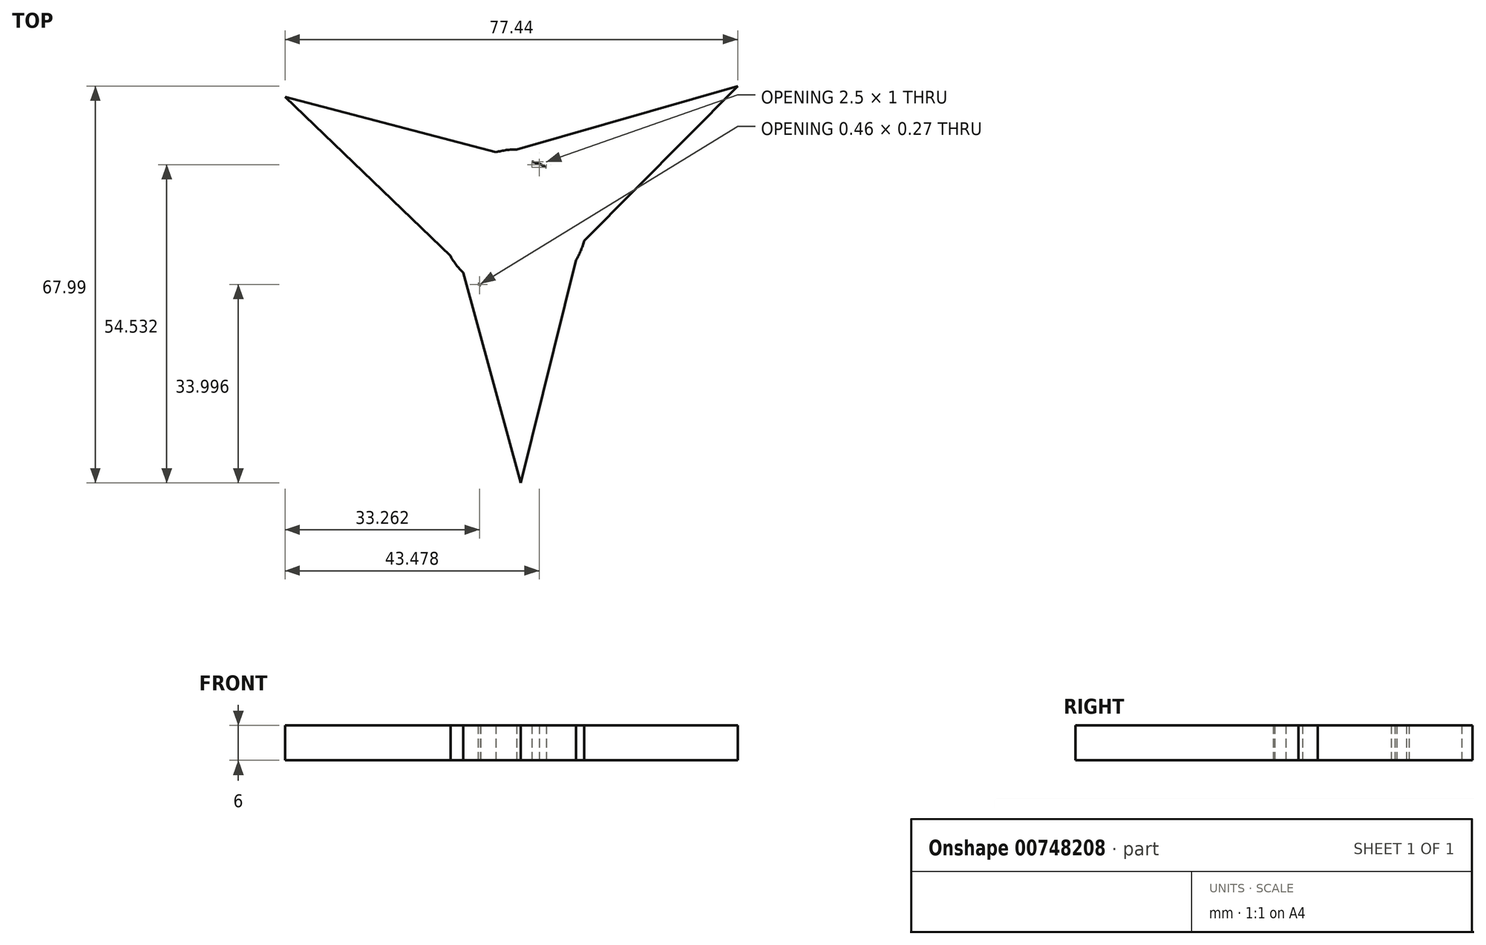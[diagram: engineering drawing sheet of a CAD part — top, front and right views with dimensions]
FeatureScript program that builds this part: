
annotation { "Feature Type Name" : "Feature", "Feature Type Description" : "" }
export const myFeature = defineFeature(function(context is Context, id is Id, definition is map)
    precondition{}
    {
        {
            var Q0;
            Q0=qCreatedBy(makeId("Top.planeOp"),FACE);
            var sketch = newSketch(context, id + "F0", { "sketchPlane" : qUnion([Q0])});
            skCircle(sketch, "E0", {"center": v(0.18, 0.31) * mm, "radius": 11 * mm});
            skCircle(sketch, "E1", {"center": v(0.18, 0.31) * mm, "radius": 12.1 * mm});
            skLineSegment(sketch, "E2", {"start": v(-5.66, -10.27) * mm, "end": v(-0.97, -34.05) * mm});
            skLineSegment(sketch, "E3", {"start": v(-0.97, -34.05) * mm, "end": v(1.1, -22.16) * mm});
            skPoint(sketch, "E3.endSnap0", {"position": v(-3.32, -22.16) * mm});
            skLineSegment(sketch, "E4", {"start": v(1.1, -22.16) * mm, "end": v(3.44, -34.05) * mm});
            skLineSegment(sketch, "E5", {"start": v(3.44, -34.05) * mm, "end": v(8.37, -5.81) * mm});
            skLineSegment(sketch, "E6", {"start": v(-11.75, 2.26) * mm, "end": v(1.06, -44.71) * mm});
            skLineSegment(sketch, "E7", {"start": v(1.06, -44.71) * mm, "end": v(12.28, 0.44) * mm});
            skLineSegment(sketch, "E8.1.0", {"start": v(38.2, 23.28) * mm, "end": v(-6.52, 10.41) * mm});
            skLineSegment(sketch, "E8.1.1", {"start": v(3.91, -11.3) * mm, "end": v(38.2, 23.28) * mm});
            skLineSegment(sketch, "E8.1.2", {"start": v(27.77, 20) * mm, "end": v(0.85, 10.15) * mm});
            skLineSegment(sketch, "E8.1.3", {"start": v(18.64, 12.03) * mm, "end": v(27.77, 20) * mm});
            skLineSegment(sketch, "E8.1.4", {"start": v(29.97, 16.18) * mm, "end": v(18.64, 12.03) * mm});
            skLineSegment(sketch, "E8.1.5", {"start": v(11.73, 0.23) * mm, "end": v(29.97, 16.18) * mm});
            skCircle(sketch, "E8.1.6", {"center": v(-0.36, 0) * mm, "radius": 12.1 * mm});
            skCircle(sketch, "E8.1.7", {"center": v(-0.36, 0) * mm, "radius": 11 * mm});
            skPoint(sketch, "E8.1.8", {"position": v(20.85, 8.2) * mm});
            skLineSegment(sketch, "E8.2.0", {"start": v(-39.25, 21.44) * mm, "end": v(-5.76, -10.85) * mm});
            skLineSegment(sketch, "E8.2.1", {"start": v(7.83, 9.04) * mm, "end": v(-39.25, 21.44) * mm});
            skLineSegment(sketch, "E8.2.2", {"start": v(-31.2, 14.04) * mm, "end": v(-9.22, -4.34) * mm});
            skLineSegment(sketch, "E8.2.3", {"start": v(-19.74, 10.13) * mm, "end": v(-31.2, 14.04) * mm});
            skLineSegment(sketch, "E8.2.4", {"start": v(-29, 17.87) * mm, "end": v(-19.74, 10.13) * mm});
            skLineSegment(sketch, "E8.2.5", {"start": v(-6.06, 10.04) * mm, "end": v(-29, 17.87) * mm});
            skCircle(sketch, "E8.2.6", {"center": v(0.18, -0.32) * mm, "radius": 12.1 * mm});
            skCircle(sketch, "E8.2.7", {"center": v(0.18, -0.32) * mm, "radius": 11 * mm});
            skPoint(sketch, "E8.2.8", {"position": v(-17.53, 13.95) * mm});
            skPoint(sketch, "E8.center", {"position": v(0, 0) * mm});
            skSolve(sketch);
        }
        {
            var Q0;
            {var subQ14=sQuery(id+"F0.wireOp",EDGE,"E8.1.3");Q0=makeQuery(id+"F0.imprint","IMPRINT",FACE,{"disambiguationData":[TD([[makeQuery(id+"F0.imprint","IMPRINT",EDGE,{"derivedFrom":subQ14}),-1.0]])]});}
            var Q1;
            {var subQ1=sQuery(id+"F0.wireOp",EDGE,"E8.1.3");Q1=makeQuery(id+"F0.imprint","IMPRINT",FACE,{"disambiguationData":[TD([[makeQuery(id+"F0.imprint","IMPRINT",EDGE,{"derivedFrom":subQ1}),1.0]])]});}
            var Q2;
            {var subQ4=sQuery(id+"F0.wireOp",EDGE,"E3");Q2=makeQuery(id+"F0.imprint","IMPRINT",FACE,{"disambiguationData":[TD([[makeQuery(id+"F0.imprint","IMPRINT",EDGE,{"derivedFrom":subQ4}),1.0]])]});}
            var Q3;
            {var subQ0=sQuery(id+"F0.wireOp",EDGE,"E8.2.3");Q3=makeQuery(id+"F0.imprint","IMPRINT",FACE,{"disambiguationData":[TD([[makeQuery(id+"F0.imprint","IMPRINT",EDGE,{"derivedFrom":subQ0}),1.0]])]});}
            var Q4;
            {var subQ1=sQuery(id+"F0.wireOp",EDGE,"E0");var subQ6=sQuery(id+"F0.wireOp",EDGE,"E8.2.7");var subQ7=makeQuery(id+"F0.imprint","INTERSECT",VERTEX,{"disambiguationData":[OD(0.0)],"derivedFrom":[subQ1,subQ6]});Q4=makeQuery(id+"F0.imprint","IMPRINT",FACE,{"disambiguationData":[TD([[makeQuery(id+"F0.imprint","IMPRINT",EDGE,{"disambiguationData":[TD([[subQ7,-1.0]])],"derivedFrom":subQ1}),1.0]])]});}
            var Q5;
            {var subQ6=sQuery(id+"F0.wireOp",EDGE,"E8.2.3");Q5=makeQuery(id+"F0.imprint","IMPRINT",FACE,{"disambiguationData":[TD([[makeQuery(id+"F0.imprint","IMPRINT",EDGE,{"derivedFrom":subQ6}),-1.0]])]});}
            var Q6;
            {var subQ0=sQuery(id+"F0.wireOp",EDGE,"E8.1.6");var subQ1=sQuery(id+"F0.wireOp",EDGE,"E6");var subQ2=makeQuery(id+"F0.imprint","INTERSECT",VERTEX,{"derivedFrom":[subQ1,subQ0]});Q6=makeQuery(id+"F0.imprint","IMPRINT",FACE,{"disambiguationData":[TD([[makeQuery(id+"F0.imprint","IMPRINT",EDGE,{"disambiguationData":[TD([[subQ2,1.0]])],"derivedFrom":subQ1}),-1.0]])]});}
            var Q7;
            {var subQ7=sQuery(id+"F0.wireOp",EDGE,"E3");Q7=makeQuery(id+"F0.imprint","IMPRINT",FACE,{"disambiguationData":[TD([[makeQuery(id+"F0.imprint","IMPRINT",EDGE,{"derivedFrom":subQ7}),-1.0]])]});}
            var Q8;
            {var subQ0=sQuery(id+"F0.wireOp",EDGE,"E8.2.2");var subQ1=sQuery(id+"F0.wireOp",EDGE,"E6");var subQ2=makeQuery(id+"F0.imprint","INTERSECT",VERTEX,{"derivedFrom":[subQ1,subQ0]});Q8=makeQuery(id+"F0.imprint","IMPRINT",FACE,{"disambiguationData":[TD([[makeQuery(id+"F0.imprint","IMPRINT",EDGE,{"disambiguationData":[TD([[subQ2,-1.0]])],"derivedFrom":subQ1}),-1.0]])]});}
            var Q9;
            {var subQ7=sQuery(id+"F0.wireOp",EDGE,"E1");var subQ8=makeQuery(id+"F0.imprint","INTERSECT",VERTEX,{"disambiguationData":[OD(0.0)],"derivedFrom":[subQ7,sQuery(id+"F0.wireOp",EDGE,"E6")]});Q9=makeQuery(id+"F0.imprint","IMPRINT",FACE,{"disambiguationData":[TD([[makeQuery(id+"F0.imprint","IMPRINT",EDGE,{"disambiguationData":[TD([[subQ8,1.0]])],"derivedFrom":subQ7}),-1.0]])]});}
            var Q10;
            {var subQ0=sQuery(id+"F0.wireOp",EDGE,"E8.1.7");var subQ1=sQuery(id+"F0.wireOp",EDGE,"E0");var subQ2=makeQuery(id+"F0.imprint","INTERSECT",VERTEX,{"disambiguationData":[OD(1.0)],"derivedFrom":[subQ1,subQ0]});Q10=makeQuery(id+"F0.imprint","IMPRINT",FACE,{"disambiguationData":[TD([[makeQuery(id+"F0.imprint","IMPRINT",EDGE,{"disambiguationData":[TD([[subQ2,-1.0]])],"derivedFrom":subQ1}),-1.0]])]});}
            var Q11;
            {var subQ0=sQuery(id+"F0.wireOp",EDGE,"E8.2.2");var subQ1=sQuery(id+"F0.wireOp",EDGE,"E0");var subQ2=makeQuery(id+"F0.imprint","INTERSECT",VERTEX,{"derivedFrom":[subQ1,subQ0]});Q11=makeQuery(id+"F0.imprint","IMPRINT",FACE,{"disambiguationData":[TD([[makeQuery(id+"F0.imprint","IMPRINT",EDGE,{"disambiguationData":[TD([[subQ2,-1.0]])],"derivedFrom":subQ1}),-1.0]])]});}
            var Q12;
            {var subQ6=sQuery(id+"F0.wireOp",EDGE,"E8.2.1");var subQ8=sQuery(id+"F0.wireOp",EDGE,"E0");var subQ9=makeQuery(id+"F0.imprint","INTERSECT",VERTEX,{"disambiguationData":[OD(0.0)],"derivedFrom":[subQ8,subQ6]});Q12=makeQuery(id+"F0.imprint","IMPRINT",FACE,{"disambiguationData":[TD([[makeQuery(id+"F0.imprint","IMPRINT",EDGE,{"disambiguationData":[TD([[subQ9,1.0]])],"derivedFrom":subQ8}),-1.0]])]});}
            var Q13;
            {var subQ0=sQuery(id+"F0.wireOp",EDGE,"E8.1.1");var subQ1=sQuery(id+"F0.wireOp",EDGE,"E1");var subQ2=makeQuery(id+"F0.imprint","INTERSECT",VERTEX,{"disambiguationData":[OD(0.0)],"derivedFrom":[subQ1,subQ0]});Q13=makeQuery(id+"F0.imprint","IMPRINT",FACE,{"disambiguationData":[TD([[makeQuery(id+"F0.imprint","IMPRINT",EDGE,{"disambiguationData":[TD([[subQ2,-1.0]])],"derivedFrom":subQ1}),-1.0]])]});}
            var Q14;
            {var subQ0=sQuery(id+"F0.wireOp",EDGE,"E7");var subQ1=sQuery(id+"F0.wireOp",EDGE,"E1");var subQ2=makeQuery(id+"F0.imprint","INTERSECT",VERTEX,{"disambiguationData":[OD(1.0)],"derivedFrom":[subQ1,subQ0]});Q14=makeQuery(id+"F0.imprint","IMPRINT",FACE,{"disambiguationData":[TD([[makeQuery(id+"F0.imprint","IMPRINT",EDGE,{"disambiguationData":[TD([[subQ2,-1.0]])],"derivedFrom":subQ1}),-1.0]])]});}
            var Q15;
            {var subQ1=sQuery(id+"F0.wireOp",EDGE,"E1");var subQ5=sQuery(id+"F0.wireOp",EDGE,"E8.1.6");var subQ6=makeQuery(id+"F0.imprint","INTERSECT",VERTEX,{"disambiguationData":[OD(1.0)],"derivedFrom":[subQ1,subQ5]});Q15=makeQuery(id+"F0.imprint","IMPRINT",FACE,{"disambiguationData":[TD([[makeQuery(id+"F0.imprint","IMPRINT",EDGE,{"disambiguationData":[TD([[subQ6,-1.0]])],"derivedFrom":subQ1}),-1.0]])]});}
            var Q16;
            {var subQ1=sQuery(id+"F0.wireOp",EDGE,"E2");var subQ6=sQuery(id+"F0.wireOp",EDGE,"E1");var subQ9=makeQuery(id+"F0.imprint","INTERSECT",VERTEX,{"derivedFrom":[subQ6,subQ1]});Q16=makeQuery(id+"F0.imprint","IMPRINT",FACE,{"disambiguationData":[TD([[makeQuery(id+"F0.imprint","IMPRINT",EDGE,{"disambiguationData":[TD([[subQ9,1.0]])],"derivedFrom":subQ6}),-1.0]])]});}
            var Q17;
            {var subQ0=sQuery(id+"F0.wireOp",EDGE,"E8.1.7");var subQ1=sQuery(id+"F0.wireOp",EDGE,"E6");var subQ2=makeQuery(id+"F0.imprint","INTERSECT",VERTEX,{"disambiguationData":[OD(0.0)],"derivedFrom":[subQ1,subQ0]});Q17=makeQuery(id+"F0.imprint","IMPRINT",FACE,{"disambiguationData":[TD([[makeQuery(id+"F0.imprint","IMPRINT",EDGE,{"disambiguationData":[TD([[subQ2,-1.0]])],"derivedFrom":subQ1}),-1.0]])]});}
            var Q18;
            {var subQ1=sQuery(id+"F0.wireOp",EDGE,"E0");var subQ7=sQuery(id+"F0.wireOp",EDGE,"E8.2.1");var subQ8=makeQuery(id+"F0.imprint","INTERSECT",VERTEX,{"disambiguationData":[OD(1.0)],"derivedFrom":[subQ1,subQ7]});Q18=makeQuery(id+"F0.imprint","IMPRINT",FACE,{"disambiguationData":[TD([[makeQuery(id+"F0.imprint","IMPRINT",EDGE,{"disambiguationData":[TD([[subQ8,-1.0]])],"derivedFrom":subQ1}),-1.0]])]});}
            var Q19;
            {var subQ1=sQuery(id+"F0.wireOp",EDGE,"E1");var subQ5=sQuery(id+"F0.wireOp",EDGE,"E8.1.1");var subQ6=makeQuery(id+"F0.imprint","INTERSECT",VERTEX,{"disambiguationData":[OD(0.0)],"derivedFrom":[subQ1,subQ5]});Q19=makeQuery(id+"F0.imprint","IMPRINT",FACE,{"disambiguationData":[TD([[makeQuery(id+"F0.imprint","IMPRINT",EDGE,{"disambiguationData":[TD([[subQ6,-1.0]])],"derivedFrom":subQ1}),1.0]])]});}
            var Q20;
            {var subQ1=sQuery(id+"F0.wireOp",EDGE,"E8.1.0");var subQ5=sQuery(id+"F0.wireOp",EDGE,"E8.1.6");var subQ6=makeQuery(id+"F0.imprint","INTERSECT",VERTEX,{"disambiguationData":[OD(1.0)],"derivedFrom":[subQ1,subQ5]});Q20=makeQuery(id+"F0.imprint","IMPRINT",FACE,{"disambiguationData":[TD([[makeQuery(id+"F0.imprint","IMPRINT",EDGE,{"disambiguationData":[TD([[subQ6,-1.0]])],"derivedFrom":subQ1}),1.0]])]});}
            var Q21;
            {var subQ0=sQuery(id+"F0.wireOp",EDGE,"E8.1.7");var subQ1=sQuery(id+"F0.wireOp",EDGE,"E0");var subQ2=makeQuery(id+"F0.imprint","INTERSECT",VERTEX,{"disambiguationData":[OD(0.0)],"derivedFrom":[subQ1,subQ0]});Q21=makeQuery(id+"F0.imprint","IMPRINT",FACE,{"disambiguationData":[TD([[makeQuery(id+"F0.imprint","IMPRINT",EDGE,{"disambiguationData":[TD([[subQ2,-1.0]])],"derivedFrom":subQ1}),-1.0]])]});}
            var Q22;
            {var subQ0=sQuery(id+"F0.wireOp",EDGE,"E8.1.6");var subQ1=sQuery(id+"F0.wireOp",EDGE,"E5");var subQ2=makeQuery(id+"F0.imprint","INTERSECT",VERTEX,{"derivedFrom":[subQ1,subQ0]});Q22=makeQuery(id+"F0.imprint","IMPRINT",FACE,{"disambiguationData":[TD([[makeQuery(id+"F0.imprint","IMPRINT",EDGE,{"disambiguationData":[TD([[subQ2,-1.0]])],"derivedFrom":subQ1}),-1.0]])]});}
            var Q23;
            {var subQ0=sQuery(id+"F0.wireOp",EDGE,"E8.2.2");var subQ1=sQuery(id+"F0.wireOp",EDGE,"E1");var subQ2=makeQuery(id+"F0.imprint","INTERSECT",VERTEX,{"derivedFrom":[subQ1,subQ0]});Q23=makeQuery(id+"F0.imprint","IMPRINT",FACE,{"disambiguationData":[TD([[makeQuery(id+"F0.imprint","IMPRINT",EDGE,{"disambiguationData":[TD([[subQ2,-1.0]])],"derivedFrom":subQ1}),-1.0]])]});}
            var Q24;
            {var subQ3=sQuery(id+"F0.wireOp",EDGE,"E8.1.7");var subQ7=sQuery(id+"F0.wireOp",EDGE,"E0");var subQ9=makeQuery(id+"F0.imprint","INTERSECT",VERTEX,{"disambiguationData":[OD(0.0)],"derivedFrom":[subQ7,subQ3]});Q24=makeQuery(id+"F0.imprint","IMPRINT",FACE,{"disambiguationData":[TD([[makeQuery(id+"F0.imprint","IMPRINT",EDGE,{"disambiguationData":[TD([[subQ9,-1.0]])],"derivedFrom":subQ7}),1.0]])]});}
            var Q25;
            {var subQ0=sQuery(id+"F0.wireOp",EDGE,"E8.1.5");var subQ1=sQuery(id+"F0.wireOp",EDGE,"E1");var subQ2=makeQuery(id+"F0.imprint","INTERSECT",VERTEX,{"derivedFrom":[subQ1,subQ0]});Q25=makeQuery(id+"F0.imprint","IMPRINT",FACE,{"disambiguationData":[TD([[makeQuery(id+"F0.imprint","IMPRINT",EDGE,{"disambiguationData":[TD([[subQ2,-1.0]])],"derivedFrom":subQ1}),1.0]])]});}
            var Q26;
            {var subQ0=sQuery(id+"F0.wireOp",EDGE,"E8.1.7");var subQ1=sQuery(id+"F0.wireOp",EDGE,"E5");var subQ2=makeQuery(id+"F0.imprint","INTERSECT",VERTEX,{"derivedFrom":[subQ1,subQ0]});Q26=makeQuery(id+"F0.imprint","IMPRINT",FACE,{"disambiguationData":[TD([[makeQuery(id+"F0.imprint","IMPRINT",EDGE,{"disambiguationData":[TD([[subQ2,1.0]])],"derivedFrom":subQ1}),1.0]])]});}
            var Q27;
            {var subQ0=sQuery(id+"F0.wireOp",EDGE,"E8.1.6");var subQ1=sQuery(id+"F0.wireOp",EDGE,"E8.1.0");var subQ2=makeQuery(id+"F0.imprint","INTERSECT",VERTEX,{"disambiguationData":[OD(1.0)],"derivedFrom":[subQ1,subQ0]});Q27=makeQuery(id+"F0.imprint","IMPRINT",FACE,{"disambiguationData":[TD([[makeQuery(id+"F0.imprint","IMPRINT",EDGE,{"disambiguationData":[TD([[subQ2,-1.0]])],"derivedFrom":subQ1}),-1.0]])]});}
            var Q28;
            {var subQ0=sQuery(id+"F0.wireOp",EDGE,"E8.1.6");var subQ1=sQuery(id+"F0.wireOp",EDGE,"E8.1.5");var subQ2=makeQuery(id+"F0.imprint","INTERSECT",VERTEX,{"derivedFrom":[subQ1,subQ0]});Q28=makeQuery(id+"F0.imprint","IMPRINT",FACE,{"disambiguationData":[TD([[makeQuery(id+"F0.imprint","IMPRINT",EDGE,{"disambiguationData":[TD([[subQ2,-1.0]])],"derivedFrom":subQ1}),1.0]])]});}
            var Q29;
            {var subQ0=sQuery(id+"F0.wireOp",EDGE,"E8.1.2");var subQ1=sQuery(id+"F0.wireOp",EDGE,"E0");var subQ2=makeQuery(id+"F0.imprint","INTERSECT",VERTEX,{"derivedFrom":[subQ1,subQ0]});Q29=makeQuery(id+"F0.imprint","IMPRINT",FACE,{"disambiguationData":[TD([[makeQuery(id+"F0.imprint","IMPRINT",EDGE,{"disambiguationData":[TD([[subQ2,-1.0]])],"derivedFrom":subQ1}),1.0]])]});}
            var Q30;
            {var subQ0=sQuery(id+"F0.wireOp",EDGE,"E8.1.6");var subQ1=sQuery(id+"F0.wireOp",EDGE,"E2");var subQ2=makeQuery(id+"F0.imprint","INTERSECT",VERTEX,{"derivedFrom":[subQ1,subQ0]});Q30=makeQuery(id+"F0.imprint","IMPRINT",FACE,{"disambiguationData":[TD([[makeQuery(id+"F0.imprint","IMPRINT",EDGE,{"disambiguationData":[TD([[subQ2,-1.0]])],"derivedFrom":subQ1}),-1.0]])]});}
            var Q31;
            {var subQ1=sQuery(id+"F0.wireOp",EDGE,"E1");var subQ5=sQuery(id+"F0.wireOp",EDGE,"E8.2.6");var subQ6=makeQuery(id+"F0.imprint","INTERSECT",VERTEX,{"disambiguationData":[OD(0.0)],"derivedFrom":[subQ1,subQ5]});Q31=makeQuery(id+"F0.imprint","IMPRINT",FACE,{"disambiguationData":[TD([[makeQuery(id+"F0.imprint","IMPRINT",EDGE,{"disambiguationData":[TD([[subQ6,-1.0]])],"derivedFrom":subQ1}),1.0]])]});}
            var Q32;
            {var subQ0=sQuery(id+"F0.wireOp",EDGE,"E7");var subQ1=sQuery(id+"F0.wireOp",EDGE,"E1");var subQ2=makeQuery(id+"F0.imprint","INTERSECT",VERTEX,{"disambiguationData":[OD(0.0)],"derivedFrom":[subQ1,subQ0]});Q32=makeQuery(id+"F0.imprint","IMPRINT",FACE,{"disambiguationData":[TD([[makeQuery(id+"F0.imprint","IMPRINT",EDGE,{"disambiguationData":[TD([[subQ2,1.0]])],"derivedFrom":subQ1}),1.0]])]});}
            var Q33;
            {var subQ0=sQuery(id+"F0.wireOp",EDGE,"E8.2.0");var subQ1=sQuery(id+"F0.wireOp",EDGE,"E8.1.6");var subQ2=makeQuery(id+"F0.imprint","INTERSECT",VERTEX,{"disambiguationData":[OD(0.0)],"derivedFrom":[subQ1,subQ0]});Q33=makeQuery(id+"F0.imprint","IMPRINT",FACE,{"disambiguationData":[TD([[makeQuery(id+"F0.imprint","IMPRINT",EDGE,{"disambiguationData":[TD([[subQ2,1.0]])],"derivedFrom":subQ1}),1.0]])]});}
            var Q34;
            {var subQ0=sQuery(id+"F0.wireOp",EDGE,"E8.2.7");var subQ1=sQuery(id+"F0.wireOp",EDGE,"E8.1.7");var subQ2=makeQuery(id+"F0.imprint","INTERSECT",VERTEX,{"disambiguationData":[OD(1.0)],"derivedFrom":[subQ1,subQ0]});Q34=makeQuery(id+"F0.imprint","IMPRINT",FACE,{"disambiguationData":[TD([[makeQuery(id+"F0.imprint","IMPRINT",EDGE,{"disambiguationData":[TD([[subQ2,-1.0]])],"derivedFrom":subQ1}),1.0]])]});}
            var Q35;
            {var subQ0=sQuery(id+"F0.wireOp",EDGE,"E5");var subQ1=sQuery(id+"F0.wireOp",EDGE,"E1");var subQ2=makeQuery(id+"F0.imprint","INTERSECT",VERTEX,{"derivedFrom":[subQ1,subQ0]});Q35=makeQuery(id+"F0.imprint","IMPRINT",FACE,{"disambiguationData":[TD([[makeQuery(id+"F0.imprint","IMPRINT",EDGE,{"disambiguationData":[TD([[subQ2,-1.0]])],"derivedFrom":subQ1}),-1.0]])]});}
            var Q36;
            {var subQ0=sQuery(id+"F0.wireOp",EDGE,"E8.2.0");var subQ1=sQuery(id+"F0.wireOp",EDGE,"E6");var subQ2=makeQuery(id+"F0.imprint","INTERSECT",VERTEX,{"derivedFrom":[subQ1,subQ0]});Q36=makeQuery(id+"F0.imprint","IMPRINT",FACE,{"disambiguationData":[TD([[makeQuery(id+"F0.imprint","IMPRINT",EDGE,{"disambiguationData":[TD([[subQ2,-1.0]])],"derivedFrom":subQ1}),1.0]])]});}
            var Q37;
            {var subQ0=sQuery(id+"F0.wireOp",EDGE,"E8.2.1");var subQ1=sQuery(id+"F0.wireOp",EDGE,"E0");var subQ2=makeQuery(id+"F0.imprint","INTERSECT",VERTEX,{"disambiguationData":[OD(0.0)],"derivedFrom":[subQ1,subQ0]});Q37=makeQuery(id+"F0.imprint","IMPRINT",FACE,{"disambiguationData":[TD([[makeQuery(id+"F0.imprint","IMPRINT",EDGE,{"disambiguationData":[TD([[subQ2,1.0]])],"derivedFrom":subQ1}),1.0]])]});}
            var Q38;
            {var subQ0=sQuery(id+"F0.wireOp",EDGE,"E8.1.6");var subQ1=sQuery(id+"F0.wireOp",EDGE,"E6");var subQ2=makeQuery(id+"F0.imprint","INTERSECT",VERTEX,{"derivedFrom":[subQ1,subQ0]});Q38=makeQuery(id+"F0.imprint","IMPRINT",FACE,{"disambiguationData":[TD([[makeQuery(id+"F0.imprint","IMPRINT",EDGE,{"disambiguationData":[TD([[subQ2,1.0]])],"derivedFrom":subQ1}),1.0]])]});}
            var Q39;
            {var subQ5=sQuery(id+"F0.wireOp",EDGE,"E8.1.1");var subQ6=sQuery(id+"F0.wireOp",EDGE,"E0");var subQ7=makeQuery(id+"F0.imprint","INTERSECT",VERTEX,{"disambiguationData":[OD(1.0)],"derivedFrom":[subQ6,subQ5]});Q39=makeQuery(id+"F0.imprint","IMPRINT",FACE,{"disambiguationData":[TD([[makeQuery(id+"F0.imprint","IMPRINT",EDGE,{"disambiguationData":[TD([[subQ7,-1.0]])],"derivedFrom":subQ6}),1.0]])]});}
            var Q40;
            {var subQ0=sQuery(id+"F0.wireOp",EDGE,"E8.2.7");var subQ1=sQuery(id+"F0.wireOp",EDGE,"E6");var subQ2=makeQuery(id+"F0.imprint","INTERSECT",VERTEX,{"disambiguationData":[OD(1.0)],"derivedFrom":[subQ1,subQ0]});Q40=makeQuery(id+"F0.imprint","IMPRINT",FACE,{"disambiguationData":[TD([[makeQuery(id+"F0.imprint","IMPRINT",EDGE,{"disambiguationData":[TD([[subQ2,-1.0]])],"derivedFrom":subQ1}),1.0]])]});}
            var Q41;
            {var subQ0=sQuery(id+"F0.wireOp",EDGE,"E8.1.1");var subQ1=sQuery(id+"F0.wireOp",EDGE,"E0");var subQ2=makeQuery(id+"F0.imprint","INTERSECT",VERTEX,{"disambiguationData":[OD(0.0)],"derivedFrom":[subQ1,subQ0]});Q41=makeQuery(id+"F0.imprint","IMPRINT",FACE,{"disambiguationData":[TD([[makeQuery(id+"F0.imprint","IMPRINT",EDGE,{"disambiguationData":[TD([[subQ2,-1.0]])],"derivedFrom":subQ1}),-1.0]])]});}
            var Q42;
            {var subQ0=sQuery(id+"F0.wireOp",EDGE,"E8.1.6");var subQ1=sQuery(id+"F0.wireOp",EDGE,"E1");var subQ2=makeQuery(id+"F0.imprint","INTERSECT",VERTEX,{"disambiguationData":[OD(1.0)],"derivedFrom":[subQ1,subQ0]});Q42=makeQuery(id+"F0.imprint","IMPRINT",FACE,{"disambiguationData":[TD([[makeQuery(id+"F0.imprint","IMPRINT",EDGE,{"disambiguationData":[TD([[subQ2,-1.0]])],"derivedFrom":subQ1}),1.0]])]});}
            var Q43;
            {var subQ0=sQuery(id+"F0.wireOp",EDGE,"E8.2.6");var subQ1=sQuery(id+"F0.wireOp",EDGE,"E1");var subQ2=makeQuery(id+"F0.imprint","INTERSECT",VERTEX,{"disambiguationData":[OD(0.0)],"derivedFrom":[subQ1,subQ0]});Q43=makeQuery(id+"F0.imprint","IMPRINT",FACE,{"disambiguationData":[TD([[makeQuery(id+"F0.imprint","IMPRINT",EDGE,{"disambiguationData":[TD([[subQ2,-1.0]])],"derivedFrom":subQ1}),-1.0]])]});}
            var Q44;
            {var subQ1=sQuery(id+"F0.wireOp",EDGE,"E0");var subQ7=sQuery(id+"F0.wireOp",EDGE,"E8.1.2");var subQ8=makeQuery(id+"F0.imprint","INTERSECT",VERTEX,{"derivedFrom":[subQ1,subQ7]});Q44=makeQuery(id+"F0.imprint","IMPRINT",FACE,{"disambiguationData":[TD([[makeQuery(id+"F0.imprint","IMPRINT",EDGE,{"disambiguationData":[TD([[subQ8,1.0]])],"derivedFrom":subQ1}),-1.0]])]});}
            var Q45;
            {var subQ0=sQuery(id+"F0.wireOp",EDGE,"E8.1.6");var subQ1=sQuery(id+"F0.wireOp",EDGE,"E1");var subQ2=makeQuery(id+"F0.imprint","INTERSECT",VERTEX,{"disambiguationData":[OD(0.0)],"derivedFrom":[subQ1,subQ0]});Q45=makeQuery(id+"F0.imprint","IMPRINT",FACE,{"disambiguationData":[TD([[makeQuery(id+"F0.imprint","IMPRINT",EDGE,{"disambiguationData":[TD([[subQ2,-1.0]])],"derivedFrom":subQ1}),1.0]])]});}
            var Q46;
            {var subQ0=sQuery(id+"F0.wireOp",EDGE,"E6");var subQ1=sQuery(id+"F0.wireOp",EDGE,"E1");var subQ2=makeQuery(id+"F0.imprint","INTERSECT",VERTEX,{"disambiguationData":[OD(0.0)],"derivedFrom":[subQ1,subQ0]});Q46=makeQuery(id+"F0.imprint","IMPRINT",FACE,{"disambiguationData":[TD([[makeQuery(id+"F0.imprint","IMPRINT",EDGE,{"disambiguationData":[TD([[subQ2,1.0]])],"derivedFrom":subQ1}),1.0]])]});}
            var Q47;
            {var subQ0=sQuery(id+"F0.wireOp",EDGE,"E8.2.6");var subQ1=sQuery(id+"F0.wireOp",EDGE,"E8.1.6");var subQ2=makeQuery(id+"F0.imprint","INTERSECT",VERTEX,{"disambiguationData":[OD(0.0)],"derivedFrom":[subQ1,subQ0]});Q47=makeQuery(id+"F0.imprint","IMPRINT",FACE,{"disambiguationData":[TD([[makeQuery(id+"F0.imprint","IMPRINT",EDGE,{"disambiguationData":[TD([[subQ2,-1.0]])],"derivedFrom":subQ1}),-1.0]])]});}
            var Q48;
            {var subQ0=sQuery(id+"F0.wireOp",EDGE,"E8.1.7");var subQ1=sQuery(id+"F0.wireOp",EDGE,"E8.1.2");var subQ2=makeQuery(id+"F0.imprint","INTERSECT",VERTEX,{"derivedFrom":[subQ1,subQ0]});Q48=makeQuery(id+"F0.imprint","IMPRINT",FACE,{"disambiguationData":[TD([[makeQuery(id+"F0.imprint","IMPRINT",EDGE,{"disambiguationData":[TD([[subQ2,-1.0]])],"derivedFrom":subQ1}),-1.0]])]});}
            var Q49;
            {var subQ0=sQuery(id+"F0.wireOp",EDGE,"E6");var subQ1=makeQuery(id+"F0.imprint","INTERSECT",VERTEX,{"derivedFrom":[sQuery(id+"F0.wireOp",EDGE,"E0"),subQ0]});Q49=makeQuery(id+"F0.imprint","IMPRINT",FACE,{"disambiguationData":[TD([[makeQuery(id+"F0.imprint","IMPRINT",EDGE,{"disambiguationData":[TD([[subQ1,1.0]])],"derivedFrom":subQ0}),-1.0]])]});}
            var Q50;
            {var subQ0=sQuery(id+"F0.wireOp",EDGE,"E8.1.6");var subQ1=sQuery(id+"F0.wireOp",EDGE,"E8.1.2");var subQ2=makeQuery(id+"F0.imprint","INTERSECT",VERTEX,{"derivedFrom":[subQ1,subQ0]});Q50=makeQuery(id+"F0.imprint","IMPRINT",FACE,{"disambiguationData":[TD([[makeQuery(id+"F0.imprint","IMPRINT",EDGE,{"disambiguationData":[TD([[subQ2,-1.0]])],"derivedFrom":subQ1}),1.0]])]});}
            var Q51;
            {var subQ0=sQuery(id+"F0.wireOp",EDGE,"E8.2.7");var subQ1=sQuery(id+"F0.wireOp",EDGE,"E8.1.2");var subQ2=makeQuery(id+"F0.imprint","INTERSECT",VERTEX,{"derivedFrom":[subQ1,subQ0]});Q51=makeQuery(id+"F0.imprint","IMPRINT",FACE,{"disambiguationData":[TD([[makeQuery(id+"F0.imprint","IMPRINT",EDGE,{"disambiguationData":[TD([[subQ2,1.0]])],"derivedFrom":subQ1}),1.0]])]});}
            var Q52;
            {var subQ0=sQuery(id+"F0.wireOp",EDGE,"E8.1.0");var subQ1=sQuery(id+"F0.wireOp",EDGE,"E1");var subQ2=makeQuery(id+"F0.imprint","INTERSECT",VERTEX,{"disambiguationData":[OD(1.0)],"derivedFrom":[subQ1,subQ0]});Q52=makeQuery(id+"F0.imprint","IMPRINT",FACE,{"disambiguationData":[TD([[makeQuery(id+"F0.imprint","IMPRINT",EDGE,{"disambiguationData":[TD([[subQ2,-1.0]])],"derivedFrom":subQ1}),-1.0]])]});}
            var Q53;
            {var subQ0=sQuery(id+"F0.wireOp",EDGE,"E8.1.0");var subQ1=sQuery(id+"F0.wireOp",EDGE,"E1");var subQ2=makeQuery(id+"F0.imprint","INTERSECT",VERTEX,{"disambiguationData":[OD(0.0)],"derivedFrom":[subQ1,subQ0]});Q53=makeQuery(id+"F0.imprint","IMPRINT",FACE,{"disambiguationData":[TD([[makeQuery(id+"F0.imprint","IMPRINT",EDGE,{"disambiguationData":[TD([[subQ2,1.0]])],"derivedFrom":subQ1}),1.0]])]});}
            var Q54;
            {var subQ0=sQuery(id+"F0.wireOp",EDGE,"E7");var subQ1=sQuery(id+"F0.wireOp",EDGE,"E1");var subQ2=makeQuery(id+"F0.imprint","INTERSECT",VERTEX,{"disambiguationData":[OD(0.0)],"derivedFrom":[subQ1,subQ0]});Q54=makeQuery(id+"F0.imprint","IMPRINT",FACE,{"disambiguationData":[TD([[makeQuery(id+"F0.imprint","IMPRINT",EDGE,{"disambiguationData":[TD([[subQ2,-1.0]])],"derivedFrom":subQ1}),1.0]])]});}
            var Q55;
            {var subQ0=sQuery(id+"F0.wireOp",EDGE,"E2");var subQ1=sQuery(id+"F0.wireOp",EDGE,"E1");var subQ2=makeQuery(id+"F0.imprint","INTERSECT",VERTEX,{"derivedFrom":[subQ1,subQ0]});Q55=makeQuery(id+"F0.imprint","IMPRINT",FACE,{"disambiguationData":[TD([[makeQuery(id+"F0.imprint","IMPRINT",EDGE,{"disambiguationData":[TD([[subQ2,-1.0]])],"derivedFrom":subQ1}),-1.0]])]});}
            var Q56;
            {var subQ0=sQuery(id+"F0.wireOp",EDGE,"E8.2.1");var subQ1=sQuery(id+"F0.wireOp",EDGE,"E0");var subQ2=makeQuery(id+"F0.imprint","INTERSECT",VERTEX,{"disambiguationData":[OD(1.0)],"derivedFrom":[subQ1,subQ0]});Q56=makeQuery(id+"F0.imprint","IMPRINT",FACE,{"disambiguationData":[TD([[makeQuery(id+"F0.imprint","IMPRINT",EDGE,{"disambiguationData":[TD([[subQ2,-1.0]])],"derivedFrom":subQ1}),1.0]])]});}
            var Q57;
            {var subQ0=sQuery(id+"F0.wireOp",EDGE,"E8.2.7");var subQ1=sQuery(id+"F0.wireOp",EDGE,"E0");var subQ2=makeQuery(id+"F0.imprint","INTERSECT",VERTEX,{"disambiguationData":[OD(0.0)],"derivedFrom":[subQ1,subQ0]});Q57=makeQuery(id+"F0.imprint","IMPRINT",FACE,{"disambiguationData":[TD([[makeQuery(id+"F0.imprint","IMPRINT",EDGE,{"disambiguationData":[TD([[subQ2,-1.0]])],"derivedFrom":subQ1}),-1.0]])]});}
            var Q58;
            {var subQ0=sQuery(id+"F0.wireOp",EDGE,"E8.1.7");var subQ1=sQuery(id+"F0.wireOp",EDGE,"E0");var subQ2=makeQuery(id+"F0.imprint","INTERSECT",VERTEX,{"disambiguationData":[OD(1.0)],"derivedFrom":[subQ1,subQ0]});Q58=makeQuery(id+"F0.imprint","IMPRINT",FACE,{"disambiguationData":[TD([[makeQuery(id+"F0.imprint","IMPRINT",EDGE,{"disambiguationData":[TD([[subQ2,-1.0]])],"derivedFrom":subQ1}),1.0]])]});}
            var Q59;
            {var subQ0=sQuery(id+"F0.wireOp",EDGE,"E5");var subQ1=sQuery(id+"F0.wireOp",EDGE,"E0");var subQ2=makeQuery(id+"F0.imprint","INTERSECT",VERTEX,{"derivedFrom":[subQ1,subQ0]});Q59=makeQuery(id+"F0.imprint","IMPRINT",FACE,{"disambiguationData":[TD([[makeQuery(id+"F0.imprint","IMPRINT",EDGE,{"disambiguationData":[TD([[subQ2,-1.0]])],"derivedFrom":subQ1}),1.0]])]});}
            var Q60;
            {var subQ0=sQuery(id+"F0.wireOp",EDGE,"E8.1.1");var subQ1=sQuery(id+"F0.wireOp",EDGE,"E0");var subQ2=makeQuery(id+"F0.imprint","INTERSECT",VERTEX,{"disambiguationData":[OD(1.0)],"derivedFrom":[subQ1,subQ0]});Q60=makeQuery(id+"F0.imprint","IMPRINT",FACE,{"disambiguationData":[TD([[makeQuery(id+"F0.imprint","IMPRINT",EDGE,{"disambiguationData":[TD([[subQ2,-1.0]])],"derivedFrom":subQ1}),-1.0]])]});}
            var Q61;
            {var subQ0=sQuery(id+"F0.wireOp",EDGE,"E6");var subQ1=sQuery(id+"F0.wireOp",EDGE,"E1");var subQ2=makeQuery(id+"F0.imprint","INTERSECT",VERTEX,{"disambiguationData":[OD(0.0)],"derivedFrom":[subQ1,subQ0]});Q61=makeQuery(id+"F0.imprint","IMPRINT",FACE,{"disambiguationData":[TD([[makeQuery(id+"F0.imprint","IMPRINT",EDGE,{"disambiguationData":[TD([[subQ2,-1.0]])],"derivedFrom":subQ1}),1.0]])]});}
            var Q62;
            {var subQ0=sQuery(id+"F0.wireOp",EDGE,"E8.2.7");var subQ1=sQuery(id+"F0.wireOp",EDGE,"E6");var subQ2=makeQuery(id+"F0.imprint","INTERSECT",VERTEX,{"disambiguationData":[OD(1.0)],"derivedFrom":[subQ1,subQ0]});Q62=makeQuery(id+"F0.imprint","IMPRINT",FACE,{"disambiguationData":[TD([[makeQuery(id+"F0.imprint","IMPRINT",EDGE,{"disambiguationData":[TD([[subQ2,-1.0]])],"derivedFrom":subQ1}),-1.0]])]});}
            var Q63;
            {var subQ0=sQuery(id+"F0.wireOp",EDGE,"E8.2.0");var subQ1=sQuery(id+"F0.wireOp",EDGE,"E6");var subQ2=makeQuery(id+"F0.imprint","INTERSECT",VERTEX,{"derivedFrom":[subQ1,subQ0]});Q63=makeQuery(id+"F0.imprint","IMPRINT",FACE,{"disambiguationData":[TD([[makeQuery(id+"F0.imprint","IMPRINT",EDGE,{"disambiguationData":[TD([[subQ2,-1.0]])],"derivedFrom":subQ1}),-1.0]])]});}
            var Q64;
            {var subQ5=sQuery(id+"F0.wireOp",EDGE,"E5");var subQ6=sQuery(id+"F0.wireOp",EDGE,"E1");var subQ7=makeQuery(id+"F0.imprint","INTERSECT",VERTEX,{"derivedFrom":[subQ6,subQ5]});Q64=makeQuery(id+"F0.imprint","IMPRINT",FACE,{"disambiguationData":[TD([[makeQuery(id+"F0.imprint","IMPRINT",EDGE,{"disambiguationData":[TD([[subQ7,-1.0]])],"derivedFrom":subQ6}),1.0]])]});}
            var Q65;
            {var subQ0=sQuery(id+"F0.wireOp",EDGE,"E7");var subQ1=sQuery(id+"F0.wireOp",EDGE,"E1");var subQ2=makeQuery(id+"F0.imprint","INTERSECT",VERTEX,{"disambiguationData":[OD(1.0)],"derivedFrom":[subQ1,subQ0]});Q65=makeQuery(id+"F0.imprint","IMPRINT",FACE,{"disambiguationData":[TD([[makeQuery(id+"F0.imprint","IMPRINT",EDGE,{"disambiguationData":[TD([[subQ2,-1.0]])],"derivedFrom":subQ1}),1.0]])]});}
            var Q66;
            {var subQ0=sQuery(id+"F0.wireOp",EDGE,"E8.1.2");var subQ1=sQuery(id+"F0.wireOp",EDGE,"E0");var subQ2=makeQuery(id+"F0.imprint","INTERSECT",VERTEX,{"derivedFrom":[subQ1,subQ0]});Q66=makeQuery(id+"F0.imprint","IMPRINT",FACE,{"disambiguationData":[TD([[makeQuery(id+"F0.imprint","IMPRINT",EDGE,{"disambiguationData":[TD([[subQ2,1.0]])],"derivedFrom":subQ1}),1.0]])]});}
            var Q67;
            {var subQ0=sQuery(id+"F0.wireOp",EDGE,"E8.1.1");var subQ1=sQuery(id+"F0.wireOp",EDGE,"E1");var subQ2=makeQuery(id+"F0.imprint","INTERSECT",VERTEX,{"disambiguationData":[OD(1.0)],"derivedFrom":[subQ1,subQ0]});Q67=makeQuery(id+"F0.imprint","IMPRINT",FACE,{"disambiguationData":[TD([[makeQuery(id+"F0.imprint","IMPRINT",EDGE,{"disambiguationData":[TD([[subQ2,-1.0]])],"derivedFrom":subQ1}),-1.0]])]});}
            var Q68;
            {var subQ1=sQuery(id+"F0.wireOp",EDGE,"E1");var subQ10=makeQuery(id+"F0.imprint","INTERSECT",VERTEX,{"derivedFrom":[subQ1,sQuery(id+"F0.wireOp",EDGE,"E2")]});Q68=makeQuery(id+"F0.imprint","IMPRINT",FACE,{"disambiguationData":[TD([[makeQuery(id+"F0.imprint","IMPRINT",EDGE,{"disambiguationData":[TD([[subQ10,1.0]])],"derivedFrom":subQ1}),1.0]])]});}
            var Q69;
            {var subQ0=sQuery(id+"F0.wireOp",EDGE,"E8.2.2");var subQ1=sQuery(id+"F0.wireOp",EDGE,"E1");var subQ2=makeQuery(id+"F0.imprint","INTERSECT",VERTEX,{"derivedFrom":[subQ1,subQ0]});Q69=makeQuery(id+"F0.imprint","IMPRINT",FACE,{"disambiguationData":[TD([[makeQuery(id+"F0.imprint","IMPRINT",EDGE,{"disambiguationData":[TD([[subQ2,-1.0]])],"derivedFrom":subQ1}),1.0]])]});}
            var Q70;
            {var subQ0=sQuery(id+"F0.wireOp",EDGE,"E8.2.2");var subQ1=sQuery(id+"F0.wireOp",EDGE,"E0");var subQ2=makeQuery(id+"F0.imprint","INTERSECT",VERTEX,{"derivedFrom":[subQ1,subQ0]});Q70=makeQuery(id+"F0.imprint","IMPRINT",FACE,{"disambiguationData":[TD([[makeQuery(id+"F0.imprint","IMPRINT",EDGE,{"disambiguationData":[TD([[subQ2,1.0]])],"derivedFrom":subQ1}),-1.0]])]});}
            var Q71;
            {var subQ0=sQuery(id+"F0.wireOp",EDGE,"E8.1.0");var subQ1=sQuery(id+"F0.wireOp",EDGE,"E1");var subQ2=makeQuery(id+"F0.imprint","INTERSECT",VERTEX,{"disambiguationData":[OD(0.0)],"derivedFrom":[subQ1,subQ0]});Q71=makeQuery(id+"F0.imprint","IMPRINT",FACE,{"disambiguationData":[TD([[makeQuery(id+"F0.imprint","IMPRINT",EDGE,{"disambiguationData":[TD([[subQ2,-1.0]])],"derivedFrom":subQ1}),1.0]])]});}
            var Q72;
            {var subQ0=sQuery(id+"F0.wireOp",EDGE,"E8.2.1");var subQ1=sQuery(id+"F0.wireOp",EDGE,"E1");var subQ2=makeQuery(id+"F0.imprint","INTERSECT",VERTEX,{"derivedFrom":[subQ1,subQ0]});Q72=makeQuery(id+"F0.imprint","IMPRINT",FACE,{"disambiguationData":[TD([[makeQuery(id+"F0.imprint","IMPRINT",EDGE,{"disambiguationData":[TD([[subQ2,-1.0]])],"derivedFrom":subQ1}),1.0]])]});}
            var Q73;
            {var subQ0=sQuery(id+"F0.wireOp",EDGE,"E8.1.6");var subQ1=sQuery(id+"F0.wireOp",EDGE,"E1");var subQ2=makeQuery(id+"F0.imprint","INTERSECT",VERTEX,{"disambiguationData":[OD(0.0)],"derivedFrom":[subQ1,subQ0]});Q73=makeQuery(id+"F0.imprint","IMPRINT",FACE,{"disambiguationData":[TD([[makeQuery(id+"F0.imprint","IMPRINT",EDGE,{"disambiguationData":[TD([[subQ2,-1.0]])],"derivedFrom":subQ1}),-1.0]])]});}
            var Q74;
            {var subQ0=sQuery(id+"F0.wireOp",EDGE,"E8.1.1");var subQ1=sQuery(id+"F0.wireOp",EDGE,"E0");var subQ2=makeQuery(id+"F0.imprint","INTERSECT",VERTEX,{"disambiguationData":[OD(0.0)],"derivedFrom":[subQ1,subQ0]});Q74=makeQuery(id+"F0.imprint","IMPRINT",FACE,{"disambiguationData":[TD([[makeQuery(id+"F0.imprint","IMPRINT",EDGE,{"disambiguationData":[TD([[subQ2,-1.0]])],"derivedFrom":subQ1}),1.0]])]});}
            var Q75;
            {var subQ0=sQuery(id+"F0.wireOp",EDGE,"E5");var subQ1=sQuery(id+"F0.wireOp",EDGE,"E0");var subQ2=makeQuery(id+"F0.imprint","INTERSECT",VERTEX,{"derivedFrom":[subQ1,subQ0]});Q75=makeQuery(id+"F0.imprint","IMPRINT",FACE,{"disambiguationData":[TD([[makeQuery(id+"F0.imprint","IMPRINT",EDGE,{"disambiguationData":[TD([[subQ2,-1.0]])],"derivedFrom":subQ1}),-1.0]])]});}
            var Q76;
            {var subQ3=sQuery(id+"F0.wireOp",EDGE,"E1");var subQ6=sQuery(id+"F0.wireOp",EDGE,"E8.1.0");var subQ9=makeQuery(id+"F0.imprint","INTERSECT",VERTEX,{"disambiguationData":[OD(1.0)],"derivedFrom":[subQ3,subQ6]});Q76=makeQuery(id+"F0.imprint","IMPRINT",FACE,{"disambiguationData":[TD([[makeQuery(id+"F0.imprint","IMPRINT",EDGE,{"disambiguationData":[TD([[subQ9,-1.0]])],"derivedFrom":subQ3}),1.0]])]});}
            var Q77;
            {var subQ0=sQuery(id+"F0.wireOp",EDGE,"E8.1.1");var subQ1=sQuery(id+"F0.wireOp",EDGE,"E1");var subQ2=makeQuery(id+"F0.imprint","INTERSECT",VERTEX,{"disambiguationData":[OD(1.0)],"derivedFrom":[subQ1,subQ0]});Q77=makeQuery(id+"F0.imprint","IMPRINT",FACE,{"disambiguationData":[TD([[makeQuery(id+"F0.imprint","IMPRINT",EDGE,{"disambiguationData":[TD([[subQ2,-1.0]])],"derivedFrom":subQ1}),1.0]])]});}
            var Q78;
            {var subQ0=sQuery(id+"F0.wireOp",EDGE,"E8.1.2");var subQ1=sQuery(id+"F0.wireOp",EDGE,"E0");var subQ2=makeQuery(id+"F0.imprint","INTERSECT",VERTEX,{"derivedFrom":[subQ1,subQ0]});Q78=makeQuery(id+"F0.imprint","IMPRINT",FACE,{"disambiguationData":[TD([[makeQuery(id+"F0.imprint","IMPRINT",EDGE,{"disambiguationData":[TD([[subQ2,-1.0]])],"derivedFrom":subQ1}),-1.0]])]});}
            var Q79;
            {var subQ0=sQuery(id+"F0.wireOp",EDGE,"E8.1.7");var subQ1=sQuery(id+"F0.wireOp",EDGE,"E8.1.2");var subQ2=makeQuery(id+"F0.imprint","INTERSECT",VERTEX,{"derivedFrom":[subQ1,subQ0]});Q79=makeQuery(id+"F0.imprint","IMPRINT",FACE,{"disambiguationData":[TD([[makeQuery(id+"F0.imprint","IMPRINT",EDGE,{"disambiguationData":[TD([[subQ2,-1.0]])],"derivedFrom":subQ1}),1.0]])]});}
            var Q80;
            {var subQ0=sQuery(id+"F0.wireOp",EDGE,"E8.2.1");var subQ1=sQuery(id+"F0.wireOp",EDGE,"E8.1.6");var subQ2=makeQuery(id+"F0.imprint","INTERSECT",VERTEX,{"disambiguationData":[OD(0.0)],"derivedFrom":[subQ1,subQ0]});Q80=makeQuery(id+"F0.imprint","IMPRINT",FACE,{"disambiguationData":[TD([[makeQuery(id+"F0.imprint","IMPRINT",EDGE,{"disambiguationData":[TD([[subQ2,-1.0]])],"derivedFrom":subQ1}),-1.0]])]});}
            var Q81;
            {var subQ3=sQuery(id+"F0.wireOp",EDGE,"E8.1.1");var subQ6=sQuery(id+"F0.wireOp",EDGE,"E7");var subQ9=makeQuery(id+"F0.imprint","INTERSECT",VERTEX,{"derivedFrom":[subQ6,subQ3]});Q81=makeQuery(id+"F0.imprint","IMPRINT",FACE,{"disambiguationData":[TD([[makeQuery(id+"F0.imprint","IMPRINT",EDGE,{"disambiguationData":[TD([[subQ9,-1.0]])],"derivedFrom":subQ6}),1.0]])]});}
            extrude(context, id + "F1", {"entities" : qUnion([Q0, Q1, Q2, Q3, Q4, Q5, Q6, Q7, Q8, Q9, Q10, Q11, Q12, Q13, Q14, Q15, Q16, Q17, Q18, Q19, Q20, Q21, Q22, Q23, Q24, Q25, Q26, Q27, Q28, Q29, Q30, Q31, Q32, Q33, Q34, Q35, Q36, Q37, Q38, Q39, Q40, Q41, Q42, Q43, Q44, Q45, Q46, Q47, Q48, Q49, Q50, Q51, Q52, Q53, Q54, Q55, Q56, Q57, Q58, Q59, Q60, Q61, Q62, Q63, Q64, Q65, Q66, Q67, Q68, Q69, Q70, Q71, Q72, Q73, Q74, Q75, Q76, Q77, Q78, Q79, Q80, Q81]), "depth" : 6 * mm, "offsetDistance" : 25 * mm});
        }
    });
